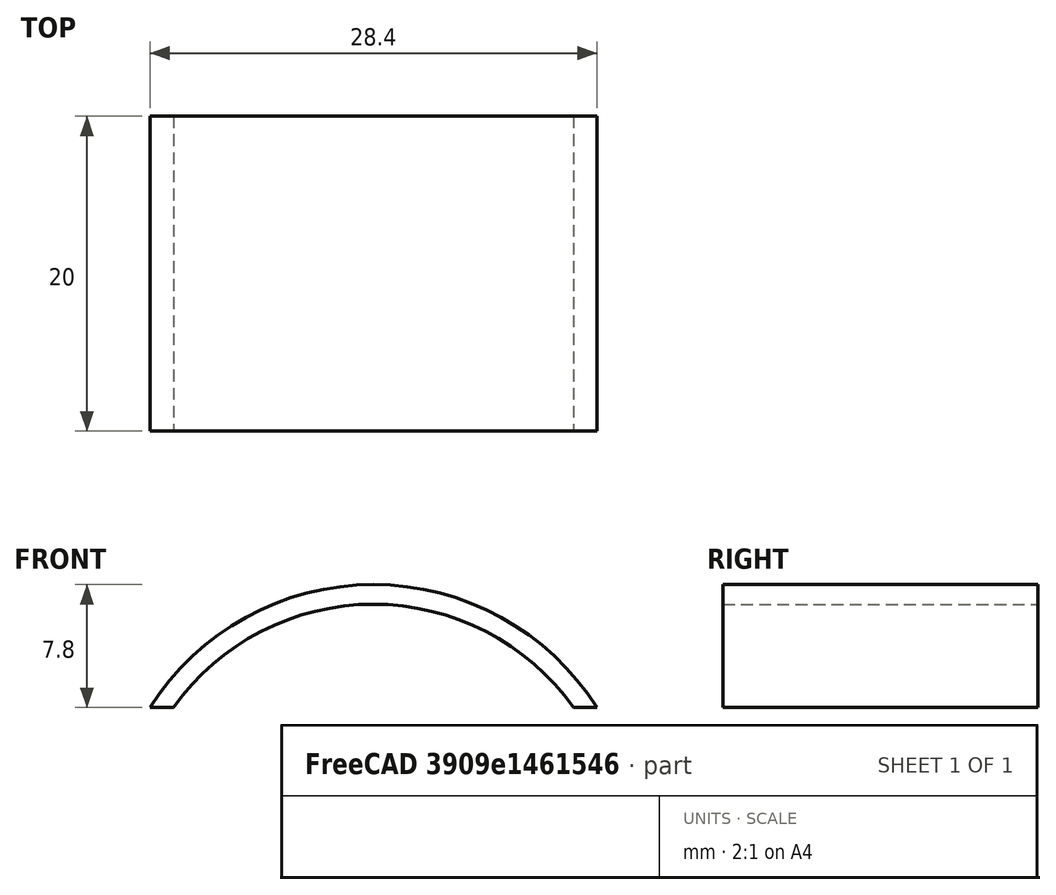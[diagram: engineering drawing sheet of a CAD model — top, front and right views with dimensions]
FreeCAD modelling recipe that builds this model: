
FCSTD DOCUMENT  (FreeCAD 0.20R29177 (Git))
Label: FlySwatterBatteryCover
License: All rights reserved
LicenseURL: http://en.wikipedia.org/wiki/All_rights_reserved
objects: Sketcher::SketchObject×1, PartDesign::Pad×1, PartDesign::Body×1
note: 4 computed .brp shape members not serialized (recipe doc carries the construction recipe); baked Part::Feature solids carry a one-line shape summary decoded from their .brp

FEATURE [Sketcher::SketchObject] Sketch
  FullyConstrained = true
  MapMode = 5
  Placement = pos=(0,0,0) rot=(1,0,0;1.5708rad)
  Support = -> [XZ_Plane]
  sketch-geometry (7):
    g0: ArcOfCircle CenterX=0 CenterY=0 CenterZ=0 NormalX=0 NormalY=0 NormalZ=1 AngleXU=0 Radius=16.8256 StartAngle=0.566192 EndAngle=2.5754
    g1: LineSegment StartX=-14.2 StartY=9.02564 StartZ=0 EndX=14.2 EndY=9.02564 EndZ=0
    g2: GeomPoint X=-6e-16 Y=9.02564 Z=0
    g3: GeomPoint X=0 Y=16.8256 Z=0
    g4: ArcOfCircle CenterX=0 CenterY=0 CenterZ=0 NormalX=0 NormalY=0 NormalZ=1 AngleXU=0 Radius=15.5805 StartAngle=0.617858 EndAngle=2.52373
    g5: LineSegment StartX=-14.2 StartY=9.02564 StartZ=0 EndX=-12.7 EndY=9.02564 EndZ=0
    g6: LineSegment StartX=12.7 StartY=9.02564 StartZ=0 EndX=14.2 EndY=9.02564 EndZ=0
  constraints (17):
    c: Coincident(g0,g-1)
    c: Distance(g0,g0) = 28.4
    c: Coincident(g1,g0)
    c: Coincident(g1,g0)
    c: Horizontal(g1)
    c: Symmetric(g0,g0,g2)
    c: PointOnObject(g3,g0)
    c: PointOnObject(g3,g-2)
    c: Distance(g3,g2) = 7.8
    c: Coincident(g4,g0)
    c: PointOnObject(g4,g1)
    c: PointOnObject(g4,g1)
    c: Distance(g0,g4) = 1.5
    c: Coincident(g5,g0)
    c: Coincident(g5,g4)
    c: Coincident(g6,g4)
    c: Coincident(g6,g0)
FEATURE [PartDesign::Pad] Pad
  Direction = (0,-1,-2e-16)
  Length = 20
  Length2 = 10
  Placement = pos=(0,0,0) rot=(1,0,0;1.5708rad)
  Profile = -> Sketch
  ReferenceAxis = -> Sketch [N_Axis]
  Type = 0
FEATURE [PartDesign::Body] Body
  Group = -> [Sketch,Pad]
  Origin = -> Origin
  Tip = -> Pad
